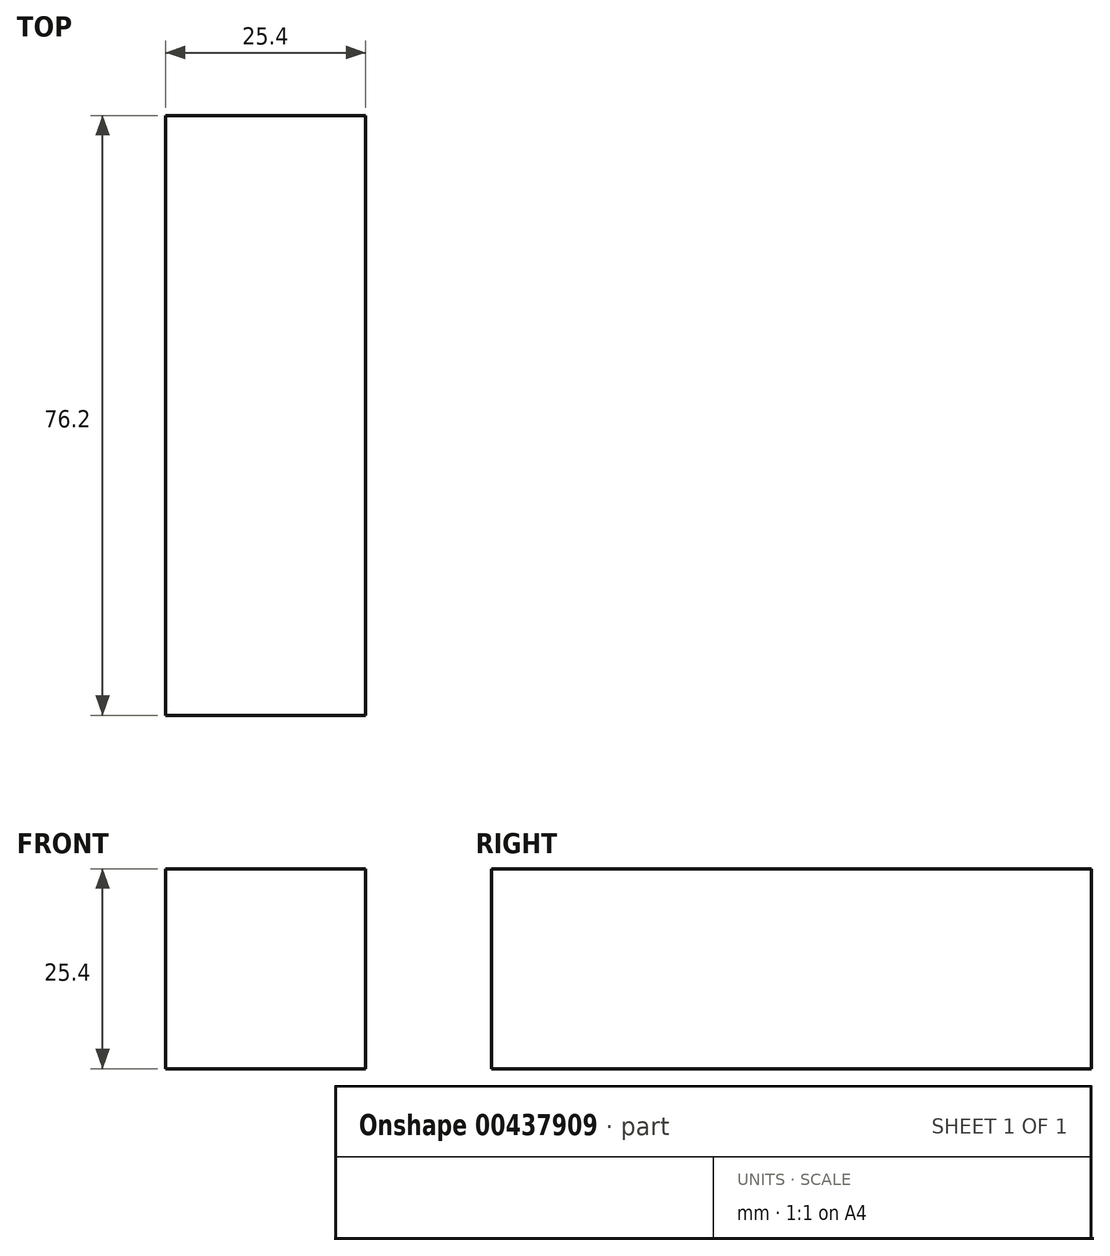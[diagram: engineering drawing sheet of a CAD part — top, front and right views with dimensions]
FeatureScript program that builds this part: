
annotation { "Feature Type Name" : "Feature", "Feature Type Description" : "" }
export const myFeature = defineFeature(function(context is Context, id is Id, definition is map)
    precondition{}
    {
        {
            var Q0;
            Q0=qCreatedBy(makeId("Front.planeOp"),FACE);
            var sketch = newSketch(context, id + "F0", { "sketchPlane" : qUnion([Q0])});
            skLineSegment(sketch, "E0.bottom", {"start": v(-13.94, 17.19) * mm, "end": v(11.46, 17.19) * mm});
            skLineSegment(sketch, "E0.top", {"start": v(-13.94, -8.21) * mm, "end": v(11.46, -8.21) * mm});
            skLineSegment(sketch, "E0.left", {"start": v(-13.94, 17.19) * mm, "end": v(-13.94, -8.21) * mm});
            skLineSegment(sketch, "E0.right", {"start": v(11.46, 17.19) * mm, "end": v(11.46, -8.21) * mm});
            skSolve(sketch);
        }
        {
            var Q0;
            Q0 = qSketchRegion(id + "F0", true);
            extrude(context, id + "F1", {"entities" : qUnion([Q0]), "depth" : 76.2 * mm});
        }
    });
